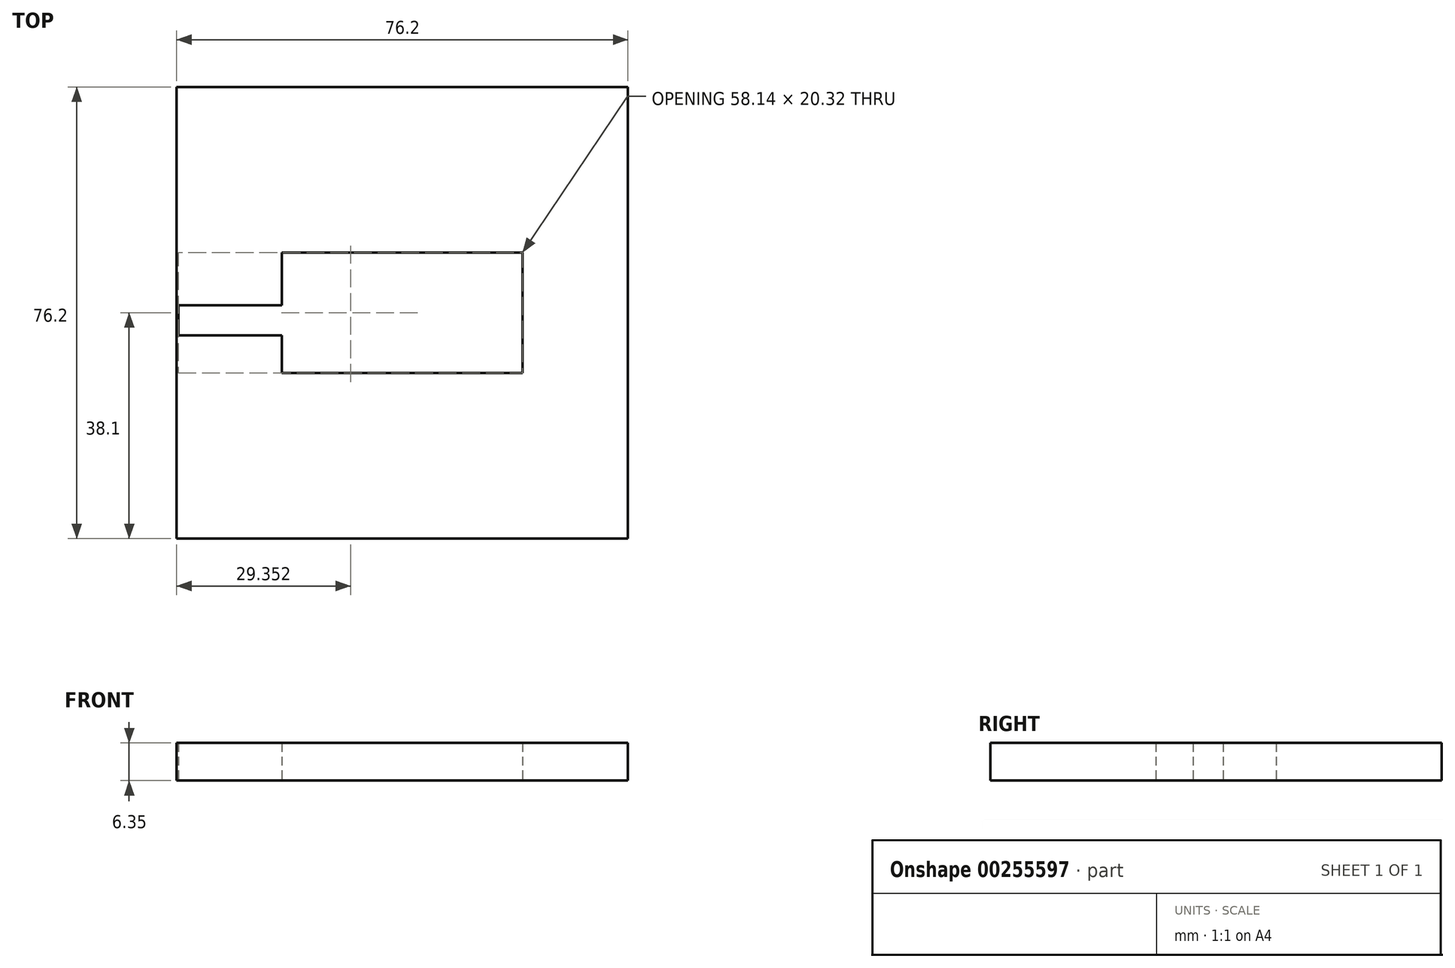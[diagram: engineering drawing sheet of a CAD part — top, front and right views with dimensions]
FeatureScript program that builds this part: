
annotation { "Feature Type Name" : "Feature", "Feature Type Description" : "" }
export const myFeature = defineFeature(function(context is Context, id is Id, definition is map)
    precondition{}
    {
        {
            var Q0;
            Q0=qCreatedBy(makeId("Top.planeOp"),FACE);
            var sketch = newSketch(context, id + "F0", { "sketchPlane" : qUnion([Q0])});
            skLineSegment(sketch, "E0.bottom", {"start": v(0, 0) * mm, "end": v(-76.2, 0) * mm});
            skLineSegment(sketch, "E0.top", {"start": v(0, -76.2) * mm, "end": v(-76.2, -76.2) * mm});
            skLineSegment(sketch, "E0.left", {"start": v(0, 0) * mm, "end": v(0, -76.2) * mm});
            skLineSegment(sketch, "E0.right", {"start": v(-76.2, 0) * mm, "end": v(-76.2, -76.2) * mm});
            skSolve(sketch);
        }
        {
            var Q0;
            Q0=makeQuery(id+"F0.imprint","IMPRINT",FACE,{"disambiguationData":[TD([[makeQuery(id+"F0.imprint","IMPRINT",EDGE,{"derivedFrom":sQuery(id+"F0.wireOp",EDGE,"E0.bottom")}),1.0]])]});
            var sketch = newSketch(context, id + "F1", { "sketchPlane" : qUnion([Q0])});
            skLineSegment(sketch, "E1.bottom", {"start": v(-17.78, -27.94) * mm, "end": v(-58.42, -27.94) * mm});
            skLineSegment(sketch, "E1.top", {"start": v(-17.78, -48.26) * mm, "end": v(-58.42, -48.26) * mm});
            skLineSegment(sketch, "E1.left", {"start": v(-17.78, -27.94) * mm, "end": v(-17.78, -48.26) * mm});
            skLineSegment(sketch, "E1.right", {"start": v(-58.42, -27.94) * mm, "end": v(-58.42, -48.26) * mm});
            skSolve(sketch);
        }
        {
            var Q0;
            Q0=makeQuery(id+"F1.imprint","IMPRINT",FACE,{"disambiguationData":[TD([[makeQuery(id+"F1.imprint","IMPRINT",EDGE,{"derivedFrom":sQuery(id+"F1.wireOp",EDGE,"E1.bottom")}),-1.0]])]});
            extrude(context, id + "F2", {"entities" : qUnion([Q0]), "depth" : 6.35 * mm});
        }
        {
            var Q0;
            Q0=makeQuery(id+"F0.imprint","IMPRINT",FACE,{"disambiguationData":[TD([[makeQuery(id+"F0.imprint","IMPRINT",EDGE,{"derivedFrom":sQuery(id+"F0.wireOp",EDGE,"E0.bottom")}),1.0]])]});
            var sketch = newSketch(context, id + "F3", { "sketchPlane" : qUnion([Q0])});
            skLineSegment(sketch, "E2.bottom", {"start": v(-58.15, -41.92) * mm, "end": v(-75.92, -41.92) * mm});
            skLineSegment(sketch, "E2.top", {"start": v(-58.15, -36.84) * mm, "end": v(-75.92, -36.84) * mm});
            skLineSegment(sketch, "E2.left", {"start": v(-58.15, -41.92) * mm, "end": v(-58.15, -36.84) * mm});
            skLineSegment(sketch, "E2.right", {"start": v(-75.92, -41.92) * mm, "end": v(-75.92, -36.84) * mm});
            skSolve(sketch);
        }
        {
            var Q0;
            Q0 = qSketchRegion(id + "F3", true);
            extrude(context, id + "F4", {"entities" : qUnion([Q0]), "operationType" : NewBodyOperationType.REMOVE, "depth" : 25.4 * mm});
        }
    });
